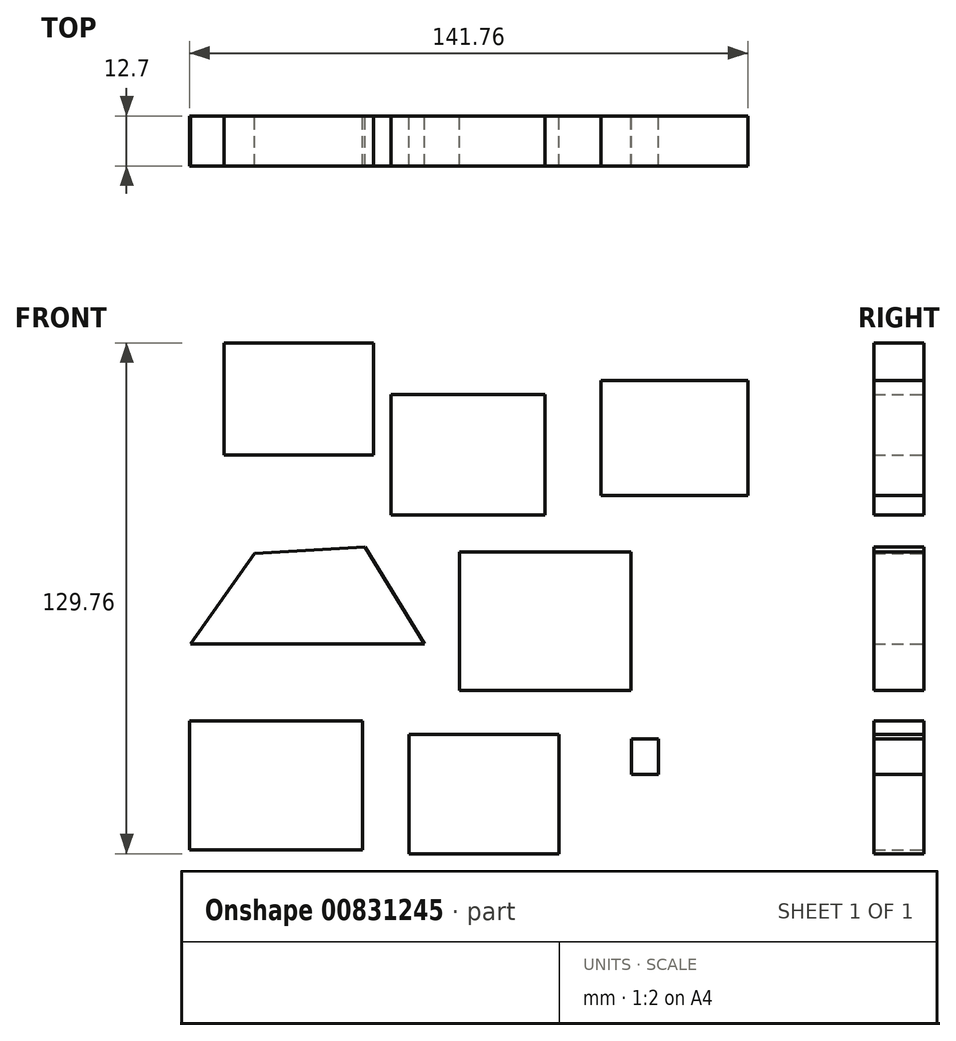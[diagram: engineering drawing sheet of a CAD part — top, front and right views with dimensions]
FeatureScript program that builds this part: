
annotation { "Feature Type Name" : "Feature", "Feature Type Description" : "" }
export const myFeature = defineFeature(function(context is Context, id is Id, definition is map)
    precondition{}
    {
        {
            var Q0;
            Q0=qCreatedBy(makeId("Front.planeOp"),FACE);
            var sketch = newSketch(context, id + "F0", { "sketchPlane" : qUnion([Q0])});
            skLineSegment(sketch, "E0.bottom", {"start": v(-25.7, 48) * mm, "end": v(-63.73, 48) * mm});
            skLineSegment(sketch, "E0.top", {"start": v(-25.7, 76.42) * mm, "end": v(-63.73, 76.42) * mm});
            skLineSegment(sketch, "E0.left", {"start": v(-25.7, 48) * mm, "end": v(-25.7, 76.42) * mm});
            skLineSegment(sketch, "E0.right", {"start": v(-63.73, 48) * mm, "end": v(-63.73, 76.42) * mm});
            skPoint(sketch, "E0.middle", {"position": v(-44.72, 62.2) * mm});
            skLineSegment(sketch, "E1.bottom", {"start": v(17.85, 63.31) * mm, "end": v(-21.28, 63.31) * mm});
            skLineSegment(sketch, "E1.top", {"start": v(17.85, 32.67) * mm, "end": v(-21.28, 32.67) * mm});
            skLineSegment(sketch, "E1.left", {"start": v(17.85, 63.31) * mm, "end": v(17.85, 32.67) * mm});
            skLineSegment(sketch, "E1.right", {"start": v(-21.28, 63.31) * mm, "end": v(-21.28, 32.67) * mm});
            skPoint(sketch, "E1.middle", {"position": v(-1.71, 48) * mm});
            skLineSegment(sketch, "E2.bottom", {"start": v(39.64, -11.81) * mm, "end": v(-3.93, -11.81) * mm});
            skLineSegment(sketch, "E2.top", {"start": v(39.64, 23.26) * mm, "end": v(-3.93, 23.26) * mm});
            skLineSegment(sketch, "E2.left", {"start": v(39.64, -11.81) * mm, "end": v(39.64, 23.26) * mm});
            skLineSegment(sketch, "E2.right", {"start": v(-3.93, -11.81) * mm, "end": v(-3.93, 23.26) * mm});
            skPoint(sketch, "E2.middle", {"position": v(17.85, 5.72) * mm});
            skLineSegment(sketch, "E3.bottom", {"start": v(-28.48, -52.42) * mm, "end": v(-72.4, -52.42) * mm});
            skLineSegment(sketch, "E3.top", {"start": v(-28.48, -19.57) * mm, "end": v(-72.4, -19.57) * mm});
            skLineSegment(sketch, "E3.left", {"start": v(-28.48, -52.42) * mm, "end": v(-28.48, -19.57) * mm});
            skLineSegment(sketch, "E3.right", {"start": v(-72.4, -52.42) * mm, "end": v(-72.4, -19.57) * mm});
            skPoint(sketch, "E3.middle", {"position": v(-50.44, -36) * mm});
            skLineSegment(sketch, "E4.bottom", {"start": v(21.36, -53.34) * mm, "end": v(-16.66, -53.34) * mm});
            skLineSegment(sketch, "E4.top", {"start": v(21.36, -23.07) * mm, "end": v(-16.66, -23.07) * mm});
            skLineSegment(sketch, "E4.left", {"start": v(21.36, -53.34) * mm, "end": v(21.36, -23.07) * mm});
            skLineSegment(sketch, "E4.right", {"start": v(-16.66, -53.34) * mm, "end": v(-16.66, -23.07) * mm});
            skPoint(sketch, "E4.middle", {"position": v(2.35, -38.2) * mm});
            skLineSegment(sketch, "E5.bottom", {"start": v(69.35, 37.65) * mm, "end": v(32.07, 37.65) * mm});
            skLineSegment(sketch, "E5.top", {"start": v(69.35, 66.82) * mm, "end": v(32.07, 66.82) * mm});
            skLineSegment(sketch, "E5.left", {"start": v(69.35, 37.65) * mm, "end": v(69.35, 66.82) * mm});
            skLineSegment(sketch, "E5.right", {"start": v(32.07, 37.65) * mm, "end": v(32.07, 66.82) * mm});
            skPoint(sketch, "E5.middle", {"position": v(50.71, 52.24) * mm});
            skLineSegment(sketch, "E6", {"start": v(-55.98, 22.89) * mm, "end": v(-72.22, 0) * mm});
            skLineSegment(sketch, "E7", {"start": v(-72.22, 0) * mm, "end": v(-12.79, 0) * mm});
            skLineSegment(sketch, "E8", {"start": v(-12.79, 0) * mm, "end": v(-27.92, 24.55) * mm});
            skLineSegment(sketch, "E9", {"start": v(-27.92, 24.55) * mm, "end": v(-55.98, 22.89) * mm});
            skLineSegment(sketch, "E10.bottom", {"start": v(46.65, -24.18) * mm, "end": v(39.82, -24.18) * mm});
            skLineSegment(sketch, "E10.top", {"start": v(46.65, -33.22) * mm, "end": v(39.82, -33.22) * mm});
            skLineSegment(sketch, "E10.left", {"start": v(46.65, -24.18) * mm, "end": v(46.65, -33.22) * mm});
            skLineSegment(sketch, "E10.right", {"start": v(39.82, -24.18) * mm, "end": v(39.82, -33.22) * mm});
            skSolve(sketch);
        }
        {
            var Q0;
            Q0=makeQuery(id+"F0.imprint","IMPRINT",FACE,{"disambiguationData":[TD([[makeQuery(id+"F0.imprint","IMPRINT",EDGE,{"derivedFrom":sQuery(id+"F0.wireOp",EDGE,"E0.bottom")}),-1.0]])]});
            var Q1;
            Q1=makeQuery(id+"F0.imprint","IMPRINT",FACE,{"disambiguationData":[TD([[makeQuery(id+"F0.imprint","IMPRINT",EDGE,{"derivedFrom":sQuery(id+"F0.wireOp",EDGE,"E3.bottom")}),-1.0]])]});
            var Q2;
            Q2=makeQuery(id+"F0.imprint","IMPRINT",FACE,{"disambiguationData":[TD([[makeQuery(id+"F0.imprint","IMPRINT",EDGE,{"derivedFrom":sQuery(id+"F0.wireOp",EDGE,"E4.bottom")}),-1.0]])]});
            var Q3;
            Q3=makeQuery(id+"F0.imprint","IMPRINT",FACE,{"disambiguationData":[TD([[makeQuery(id+"F0.imprint","IMPRINT",EDGE,{"derivedFrom":sQuery(id+"F0.wireOp",EDGE,"E10.bottom")}),1.0]])]});
            var Q4;
            Q4=makeQuery(id+"F0.imprint","IMPRINT",FACE,{"disambiguationData":[TD([[makeQuery(id+"F0.imprint","IMPRINT",EDGE,{"derivedFrom":sQuery(id+"F0.wireOp",EDGE,"E2.bottom")}),-1.0]])]});
            var Q5;
            Q5=makeQuery(id+"F0.imprint","IMPRINT",FACE,{"disambiguationData":[TD([[makeQuery(id+"F0.imprint","IMPRINT",EDGE,{"derivedFrom":sQuery(id+"F0.wireOp",EDGE,"E1.bottom")}),1.0]])]});
            var Q6;
            Q6=makeQuery(id+"F0.imprint","IMPRINT",FACE,{"disambiguationData":[TD([[makeQuery(id+"F0.imprint","IMPRINT",EDGE,{"derivedFrom":sQuery(id+"F0.wireOp",EDGE,"E5.bottom")}),-1.0]])]});
            var Q7;
            Q7=makeQuery(id+"F0.imprint","IMPRINT",FACE,{"disambiguationData":[TD([[makeQuery(id+"F0.imprint","IMPRINT",EDGE,{"derivedFrom":sQuery(id+"F0.wireOp",EDGE,"E6")}),1.0]])]});
            extrude(context, id + "F1", {"entities" : qUnion([Q0, Q1, Q2, Q3, Q4, Q5, Q6, Q7]), "depth" : 12.7 * mm, "offsetDistance" : 25.4 * mm});
        }
    });
